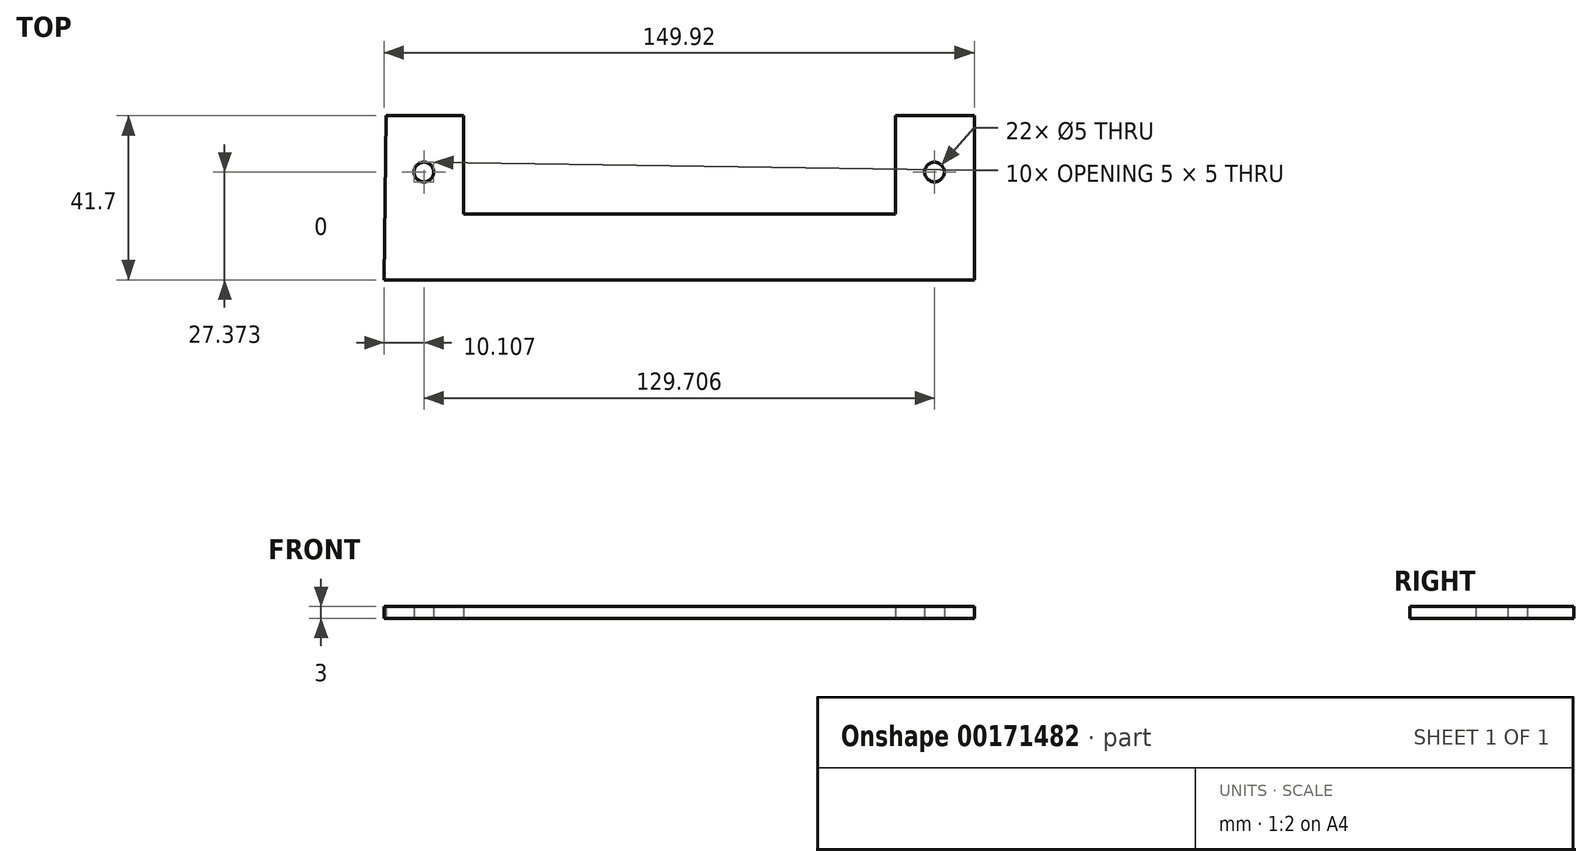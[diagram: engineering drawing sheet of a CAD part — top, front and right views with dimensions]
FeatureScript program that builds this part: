
annotation { "Feature Type Name" : "Feature", "Feature Type Description" : "" }
export const myFeature = defineFeature(function(context is Context, id is Id, definition is map)
    precondition{}
    {
        {
            var Q0;
            Q0=qCreatedBy(makeId("Top.planeOp"),FACE);
            var sketch = newSketch(context, id + "F0", { "sketchPlane" : qUnion([Q0])});
            skLineSegment(sketch, "E0", {"start": v(-74.96, 0) * mm, "end": v(74.96, 0) * mm});
            skLineSegment(sketch, "E1", {"start": v(74.96, 0) * mm, "end": v(74.96, 41.7) * mm});
            skLineSegment(sketch, "E2", {"start": v(74.96, 41.7) * mm, "end": v(54.96, 41.7) * mm});
            skLineSegment(sketch, "E3", {"start": v(54.96, 41.7) * mm, "end": v(54.96, 16.7) * mm});
            skLineSegment(sketch, "E4", {"start": v(54.96, 16.7) * mm, "end": v(-54.73, 16.7) * mm});
            skLineSegment(sketch, "E5", {"start": v(-54.73, 16.7) * mm, "end": v(-54.73, 41.7) * mm});
            skLineSegment(sketch, "E6", {"start": v(-54.73, 41.7) * mm, "end": v(-74.4, 41.7) * mm});
            skLineSegment(sketch, "E7", {"start": v(-74.4, 41.7) * mm, "end": v(-74.96, 0) * mm});
            skPoint(sketch, "E8", {"position": v(-64.85, 27.37) * mm});
            skPoint(sketch, "E9.MirrorP", {"position": v(64.85, 27.37) * mm});
            skSolve(sketch);
        }
        {
            var Q0;
            Q0=makeQuery(id+"F0.imprint","IMPRINT",FACE,{"disambiguationData":[TD([[makeQuery(id+"F0.imprint","IMPRINT",EDGE,{"derivedFrom":sQuery(id+"F0.wireOp",EDGE,"E0")}),1.0]])]});
            extrude(context, id + "F1", {"entities" : qUnion([Q0]), "depth" : 3 * mm});
        }
        {
            var Q0;
            Q0=sQuery(id+"F0.wireOp",VERTEX,"E8");
            var Q1;
            Q1=sQuery(id+"F0.wireOp",VERTEX,"E9.MirrorP");
            var Q2;
            Q2=makeQuery(id+"F1.opExtrude","SWEPT_BODY",BODY,{"disambiguationData":[OSD([sQuery(id+"F0.wireOp",EDGE,"E0"),sQuery(id+"F0.wireOp",EDGE,"E1"),sQuery(id+"F0.wireOp",EDGE,"E2"),sQuery(id+"F0.wireOp",EDGE,"E3"),sQuery(id+"F0.wireOp",EDGE,"E4"),sQuery(id+"F0.wireOp",EDGE,"E5"),sQuery(id+"F0.wireOp",EDGE,"E6"),sQuery(id+"F0.wireOp",EDGE,"E7")])]});
            hole(context, id + "F2", {"style" : HoleStyle.SIMPLE, "endStyle" : HoleEndStyle.BLIND, "oppositeDirection" : true, "holeDiameter" : 5 * mm, "holeDepth" : 50 * mm, "startFromSketch" : true, "locations" : qUnion([Q0, Q1]), "scope" : qUnion([Q2])});
        }
    });
